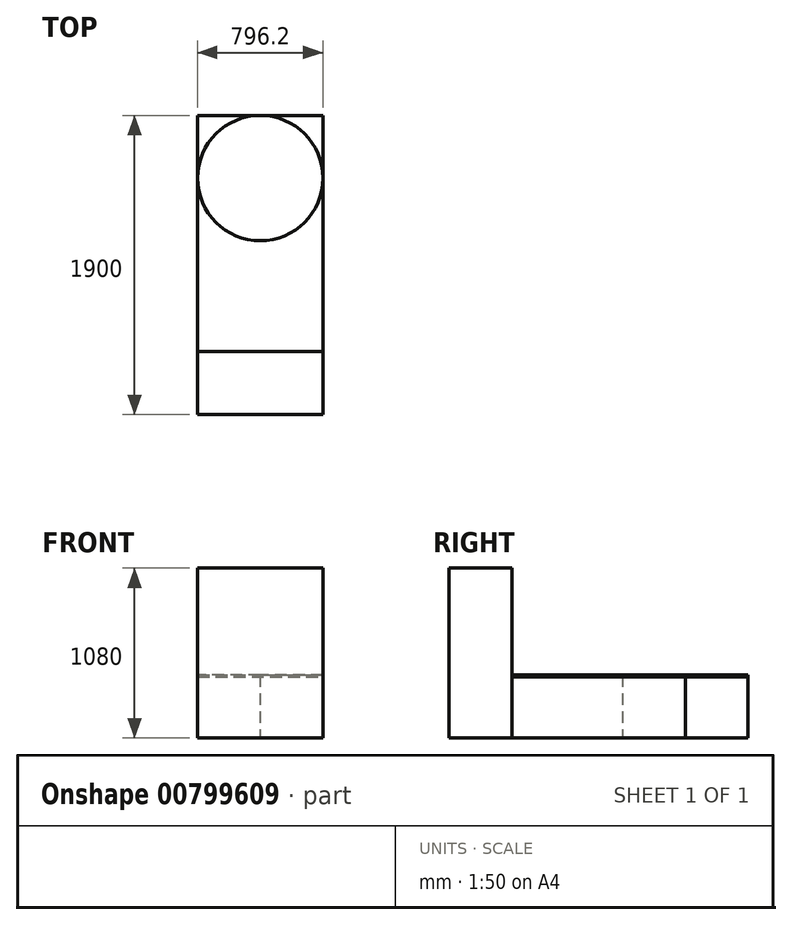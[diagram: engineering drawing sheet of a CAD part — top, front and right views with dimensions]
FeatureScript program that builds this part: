
annotation { "Feature Type Name" : "Feature", "Feature Type Description" : "" }
export const myFeature = defineFeature(function(context is Context, id is Id, definition is map)
    precondition{}
    {
        {
            var Q0;
            Q0=qCreatedBy(makeId("Top.planeOp"),FACE);
            var sketch = newSketch(context, id + "F0", { "sketchPlane" : qUnion([Q0])});
            skCircle(sketch, "E0", {"center": v(0, 0) * mm, "radius": 398.1 * mm});
            skLineSegment(sketch, "E1.bottom", {"start": v(-398.1, 398.1) * mm, "end": v(398.1, 398.1) * mm});
            skLineSegment(sketch, "E1.top", {"start": v(-398.1, -1101.9) * mm, "end": v(398.1, -1101.9) * mm});
            skLineSegment(sketch, "E1.left", {"start": v(-398.1, 398.1) * mm, "end": v(-398.1, -1101.9) * mm});
            skLineSegment(sketch, "E1.right", {"start": v(398.1, 398.1) * mm, "end": v(398.1, -1101.9) * mm});
            skSolve(sketch);
        }
        {
            var Q0;
            {var subQ5=sQuery(id+"F0.wireOp",EDGE,"E1.top");Q0=makeQuery(id+"F0.imprint","IMPRINT",FACE,{"disambiguationData":[TD([[makeQuery(id+"F0.imprint","IMPRINT",EDGE,{"derivedFrom":subQ5}),1.0]])]});}
            var Q1;
            {var subQ0=sQuery(id+"F0.wireOp",EDGE,"E1.bottom");var subQ1=sQuery(id+"F0.wireOp",EDGE,"E0");var subQ2=makeQuery(id+"F0.imprint","INTERSECT",VERTEX,{"derivedFrom":[subQ1,subQ0]});Q1=makeQuery(id+"F0.imprint","IMPRINT",FACE,{"disambiguationData":[TD([[makeQuery(id+"F0.imprint","IMPRINT",EDGE,{"disambiguationData":[TD([[subQ2,1.0]])],"derivedFrom":subQ1}),-1.0]])]});}
            var Q2;
            {var subQ0=sQuery(id+"F0.wireOp",EDGE,"E1.bottom");var subQ1=sQuery(id+"F0.wireOp",EDGE,"E0");var subQ2=makeQuery(id+"F0.imprint","INTERSECT",VERTEX,{"derivedFrom":[subQ1,subQ0]});Q2=makeQuery(id+"F0.imprint","IMPRINT",FACE,{"disambiguationData":[TD([[makeQuery(id+"F0.imprint","IMPRINT",EDGE,{"disambiguationData":[TD([[subQ2,-1.0]])],"derivedFrom":subQ1}),-1.0]])]});}
            extrude(context, id + "F1", {"entities" : qUnion([Q0, Q1, Q2]), "depth" : 400 * mm, "offsetDistance" : 25 * mm});
        }
        {
            var Q0;
            Q0 = qSketchRegion(id + "F0", true);
            extrude(context, id + "F2", {"entities" : qUnion([Q0]), "depth" : 390 * mm, "offsetDistance" : 25 * mm});
        }
        {
            var Q0;
            Q0=qCreatedBy(makeId("Top.planeOp"),FACE);
            var sketch = newSketch(context, id + "F3", { "sketchPlane" : qUnion([Q0])});
            skLineSegment(sketch, "E2.0", {"start": v(-398.1, -1101.9) * mm, "end": v(398.1, -1101.9) * mm});
            skLineSegment(sketch, "E3.top", {"start": v(-398.1, -1501.9) * mm, "end": v(398.1, -1501.9) * mm});
            skLineSegment(sketch, "E3.left", {"start": v(-398.1, -1101.9) * mm, "end": v(-398.1, -1501.9) * mm});
            skLineSegment(sketch, "E3.right", {"start": v(398.1, -1101.9) * mm, "end": v(398.1, -1501.9) * mm});
            skSolve(sketch);
        }
        {
            var Q0;
            Q0=makeQuery(id+"F3.imprint","IMPRINT",FACE,{"disambiguationData":[TD([[makeQuery(id+"F3.imprint","IMPRINT",EDGE,{"derivedFrom":sQuery(id+"F3.wireOp",EDGE,"E2.0")}),-1.0]])]});
            extrude(context, id + "F4", {"entities" : qUnion([Q0]), "depth" : 1080 * mm, "offsetDistance" : 25 * mm});
        }
    });
